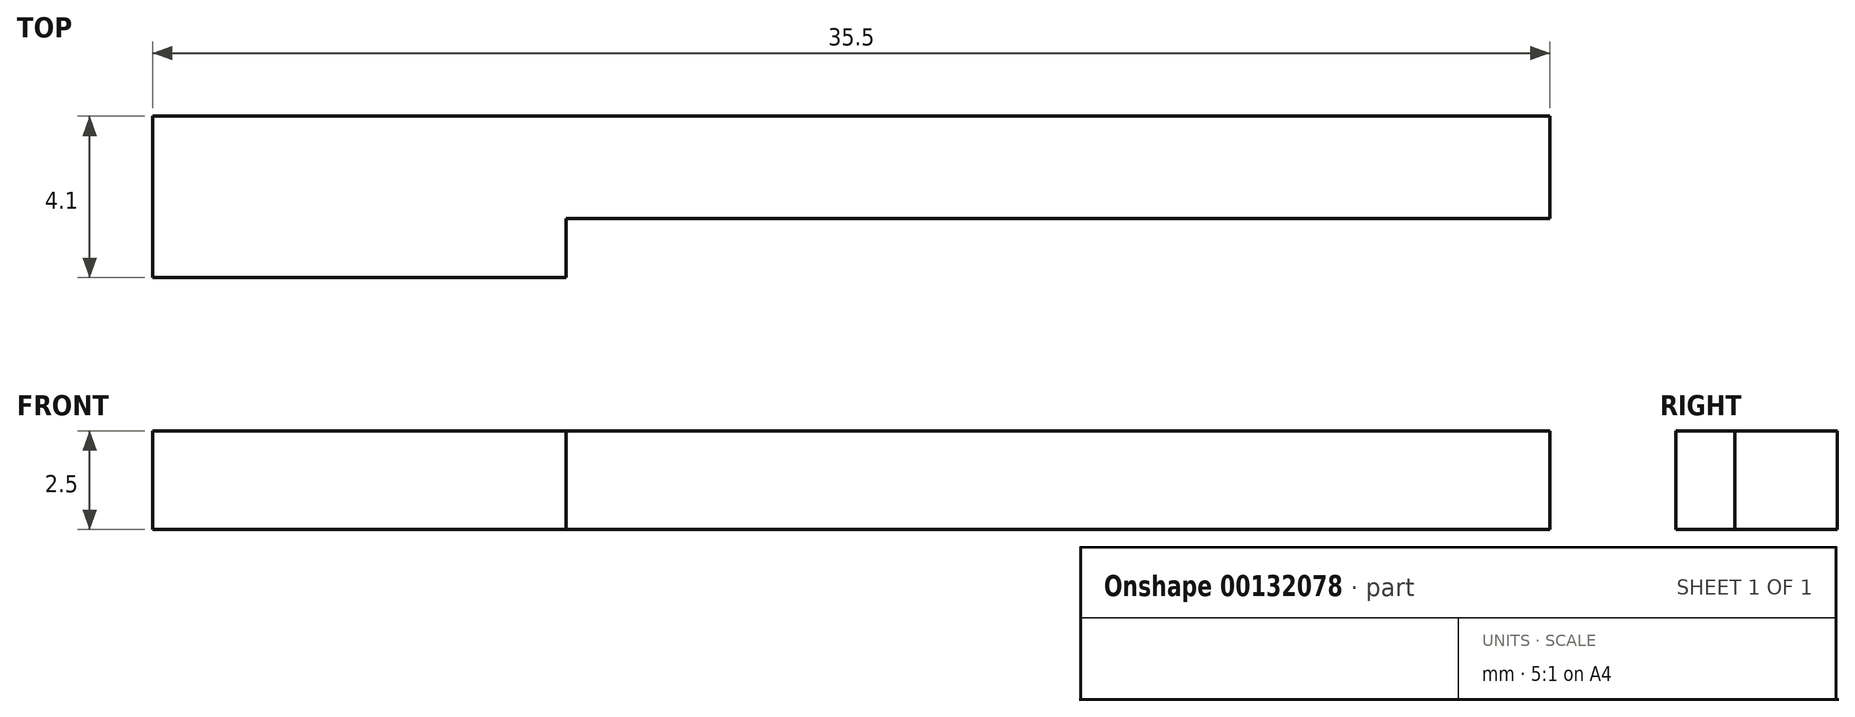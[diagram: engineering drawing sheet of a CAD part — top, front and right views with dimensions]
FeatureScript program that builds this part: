
annotation { "Feature Type Name" : "Feature", "Feature Type Description" : "" }
export const myFeature = defineFeature(function(context is Context, id is Id, definition is map)
    precondition{}
    {
        {
            var Q0;
            Q0=qCreatedBy(makeId("Top.planeOp"),FACE);
            var sketch = newSketch(context, id + "F0", { "sketchPlane" : qUnion([Q0])});
            skLineSegment(sketch, "E0.bottom", {"start": v(-31.6, 39.17) * mm, "end": v(-42.1, 39.17) * mm});
            skLineSegment(sketch, "E0.top", {"start": v(-31.6, 35.07) * mm, "end": v(-42.1, 35.07) * mm});
            skLineSegment(sketch, "E0.left", {"start": v(-31.6, 39.17) * mm, "end": v(-31.6, 35.07) * mm});
            skLineSegment(sketch, "E0.right", {"start": v(-42.1, 39.17) * mm, "end": v(-42.1, 35.07) * mm});
            skPoint(sketch, "E0.middle", {"position": v(-36.85, 37.12) * mm});
            skLineSegment(sketch, "E1.bottom", {"start": v(-31.6, 39.17) * mm, "end": v(-6.6, 39.17) * mm});
            skLineSegment(sketch, "E1.top", {"start": v(-31.6, 36.57) * mm, "end": v(-6.6, 36.57) * mm});
            skLineSegment(sketch, "E1.left", {"start": v(-31.6, 39.17) * mm, "end": v(-31.6, 36.57) * mm});
            skLineSegment(sketch, "E1.right", {"start": v(-6.6, 39.17) * mm, "end": v(-6.6, 36.57) * mm});
            skSolve(sketch);
        }
        {
            var Q0;
            Q0 = qSketchRegion(id + "F0", true);
            extrude(context, id + "F1", {"entities" : qUnion([Q0]), "depth" : 2.5 * mm});
        }
    });
